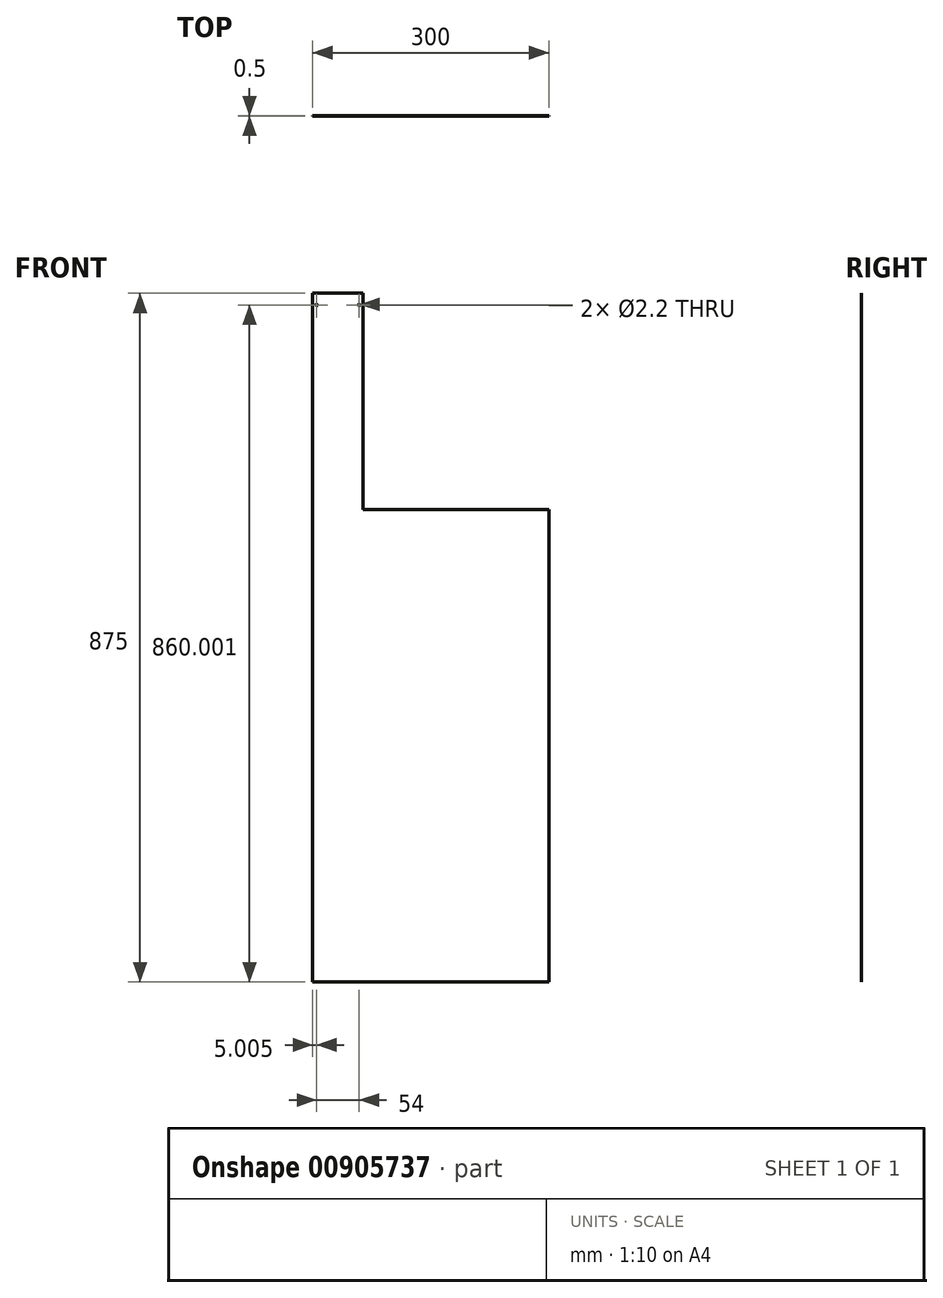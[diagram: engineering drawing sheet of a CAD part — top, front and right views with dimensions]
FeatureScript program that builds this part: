
annotation { "Feature Type Name" : "Feature", "Feature Type Description" : "" }
export const myFeature = defineFeature(function(context is Context, id is Id, definition is map)
    precondition{}
    {
        {
            var Q0;
            Q0=qCreatedBy(makeId("Front.planeOp"),FACE);
            var sketch = newSketch(context, id + "F0", { "sketchPlane" : qUnion([Q0])});
            skLineSegment(sketch, "E0.bottom", {"start": v(-196.5, 126.71) * mm, "end": v(39.5, 126.71) * mm});
            skLineSegment(sketch, "E0.top", {"start": v(-260.5, -473.29) * mm, "end": v(39.5, -473.29) * mm});
            skLineSegment(sketch, "E0.left", {"start": v(-260.5, 126.71) * mm, "end": v(-260.5, -473.29) * mm});
            skLineSegment(sketch, "E0.right", {"start": v(39.5, 126.71) * mm, "end": v(39.5, -473.29) * mm});
            skLineSegment(sketch, "E1.top", {"start": v(-260.5, 401.71) * mm, "end": v(-196.5, 401.71) * mm});
            skLineSegment(sketch, "E1.left", {"start": v(-260.5, 126.71) * mm, "end": v(-260.5, 401.71) * mm});
            skLineSegment(sketch, "E1.right", {"start": v(-196.5, 126.71) * mm, "end": v(-196.5, 401.71) * mm});
            skSolve(sketch);
        }
        {
            var Q0;
            Q0 = qSketchRegion(id + "F0", true);
            extrude(context, id + "F1", {"entities" : qUnion([Q0]), "depth" : 0.5 * mm, "offsetDistance" : 25 * mm});
        }
        {
            var Q0;
            Q0=makeQuery(id+"F1.opExtrude","CAP_FACE",FACE,{"disambiguationData":[OSD([sQuery(id+"F0.wireOp",EDGE,"E0.bottom"),sQuery(id+"F0.wireOp",EDGE,"E0.top"),sQuery(id+"F0.wireOp",EDGE,"E0.left"),sQuery(id+"F0.wireOp",EDGE,"E0.right"),sQuery(id+"F0.wireOp",EDGE,"E1.top"),sQuery(id+"F0.wireOp",EDGE,"E1.left"),sQuery(id+"F0.wireOp",EDGE,"E1.right")])],"isStart":false});
            var sketch = newSketch(context, id + "F2", { "sketchPlane" : qUnion([Q0])});
            skCircle(sketch, "E2", {"center": v(-255.5, 386.71) * mm, "radius": 1.1 * mm});
            skCircle(sketch, "E3", {"center": v(-201.5, 386.71) * mm, "radius": 1.1 * mm});
            skSolve(sketch);
        }
        {
            var Q0;
            Q0 = qSketchRegion(id + "F2", true);
            extrude(context, id + "F3", {"entities" : qUnion([Q0]), "operationType" : NewBodyOperationType.REMOVE, "endBound" : BoundingType.THROUGH_ALL, "oppositeDirection" : true, "depth" : 25 * mm, "offsetDistance" : 25 * mm});
        }
    });
